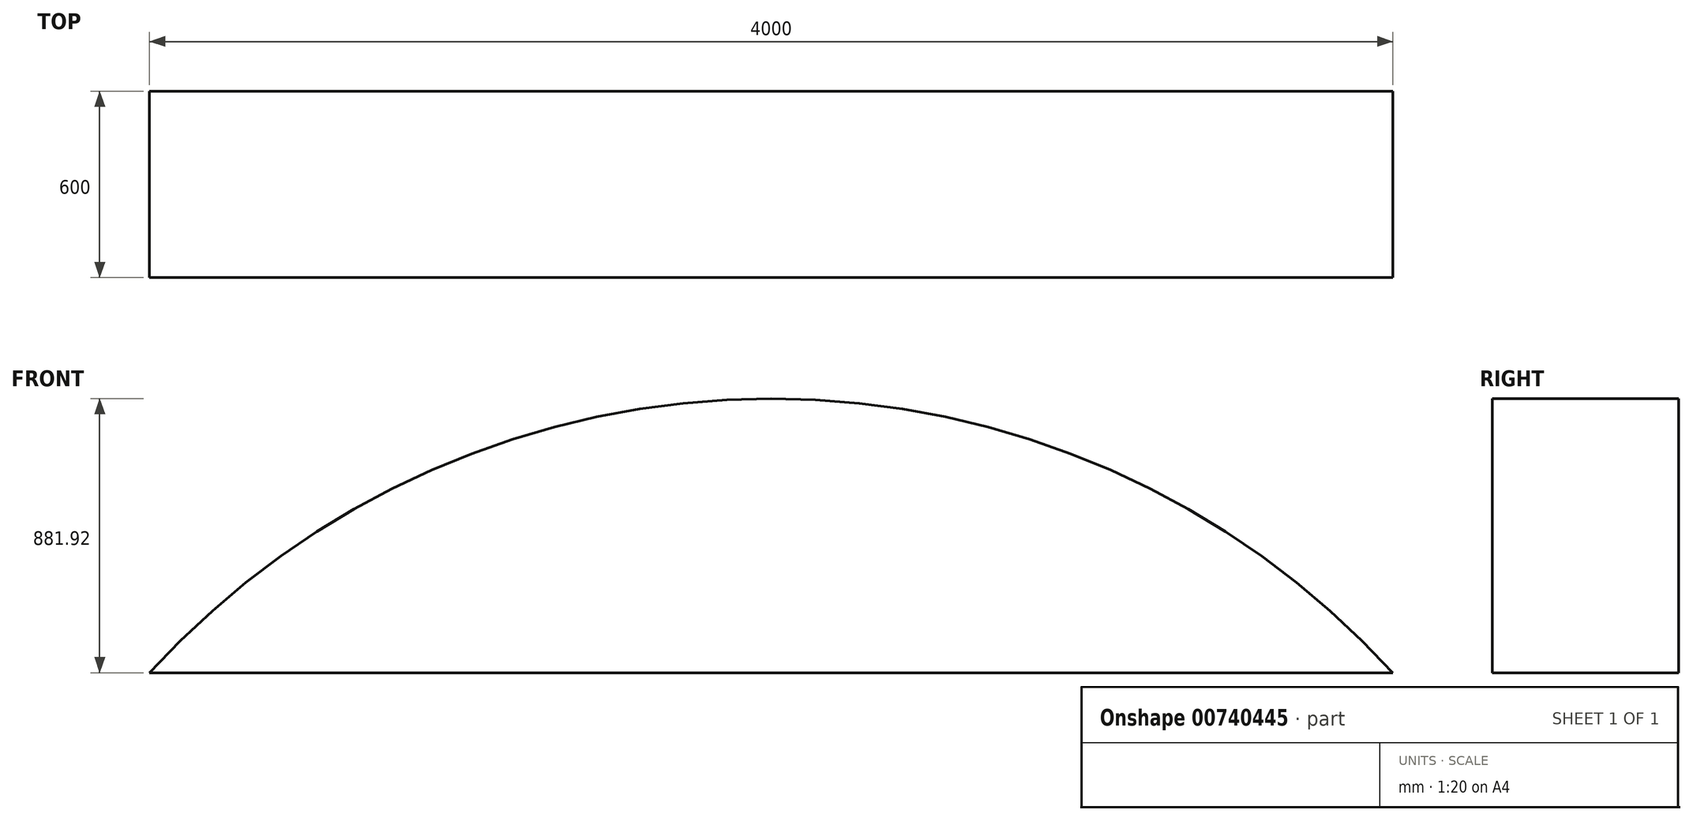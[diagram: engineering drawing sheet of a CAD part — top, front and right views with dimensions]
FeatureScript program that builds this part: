
annotation { "Feature Type Name" : "Feature", "Feature Type Description" : "" }
export const myFeature = defineFeature(function(context is Context, id is Id, definition is map)
    precondition{}
    {
        {
            var Q0;
            Q0=qCreatedBy(makeId("Top.planeOp"),FACE);
            var sketch = newSketch(context, id + "F0", { "sketchPlane" : qUnion([Q0])});
            skLineSegment(sketch, "E0.bottom", {"start": v(2000, 300) * mm, "end": v(-2000, 300) * mm});
            skLineSegment(sketch, "E0.top", {"start": v(2000, -300) * mm, "end": v(-2000, -300) * mm});
            skLineSegment(sketch, "E0.left", {"start": v(2000, 300) * mm, "end": v(2000, -300) * mm});
            skLineSegment(sketch, "E0.right", {"start": v(-2000, 300) * mm, "end": v(-2000, -300) * mm});
            skPoint(sketch, "E0.middle", {"position": v(0, 0) * mm});
            skSolve(sketch);
        }
        {
            var Q0;
            Q0=qCreatedBy(makeId("Front.planeOp"),FACE);
            var sketch = newSketch(context, id + "F1", { "sketchPlane" : qUnion([Q0])});
            skLineSegment(sketch, "E1.0", {"start": v(2000, 0) * mm, "end": v(-2000, 0) * mm});
            skArc(sketch, "E2", {"start": v(2000, 0) * mm, "mid": v(0, 881.92) * mm, "end": v(-2000, 0) * mm});
            skSolve(sketch);
        }
        {
            var Q0;
            Q0=makeQuery(id+"F1.imprint","IMPRINT",FACE,{"disambiguationData":[TD([[makeQuery(id+"F1.imprint","IMPRINT",EDGE,{"derivedFrom":sQuery(id+"F1.wireOp",EDGE,"E1.0")}),-1.0]])]});
            extrude(context, id + "F2", {"entities" : qUnion([Q0]), "oppositeDirection" : true, "depth" : 600 * mm, "offsetDistance" : 25 * mm, "symmetric" : true});
        }
    });
